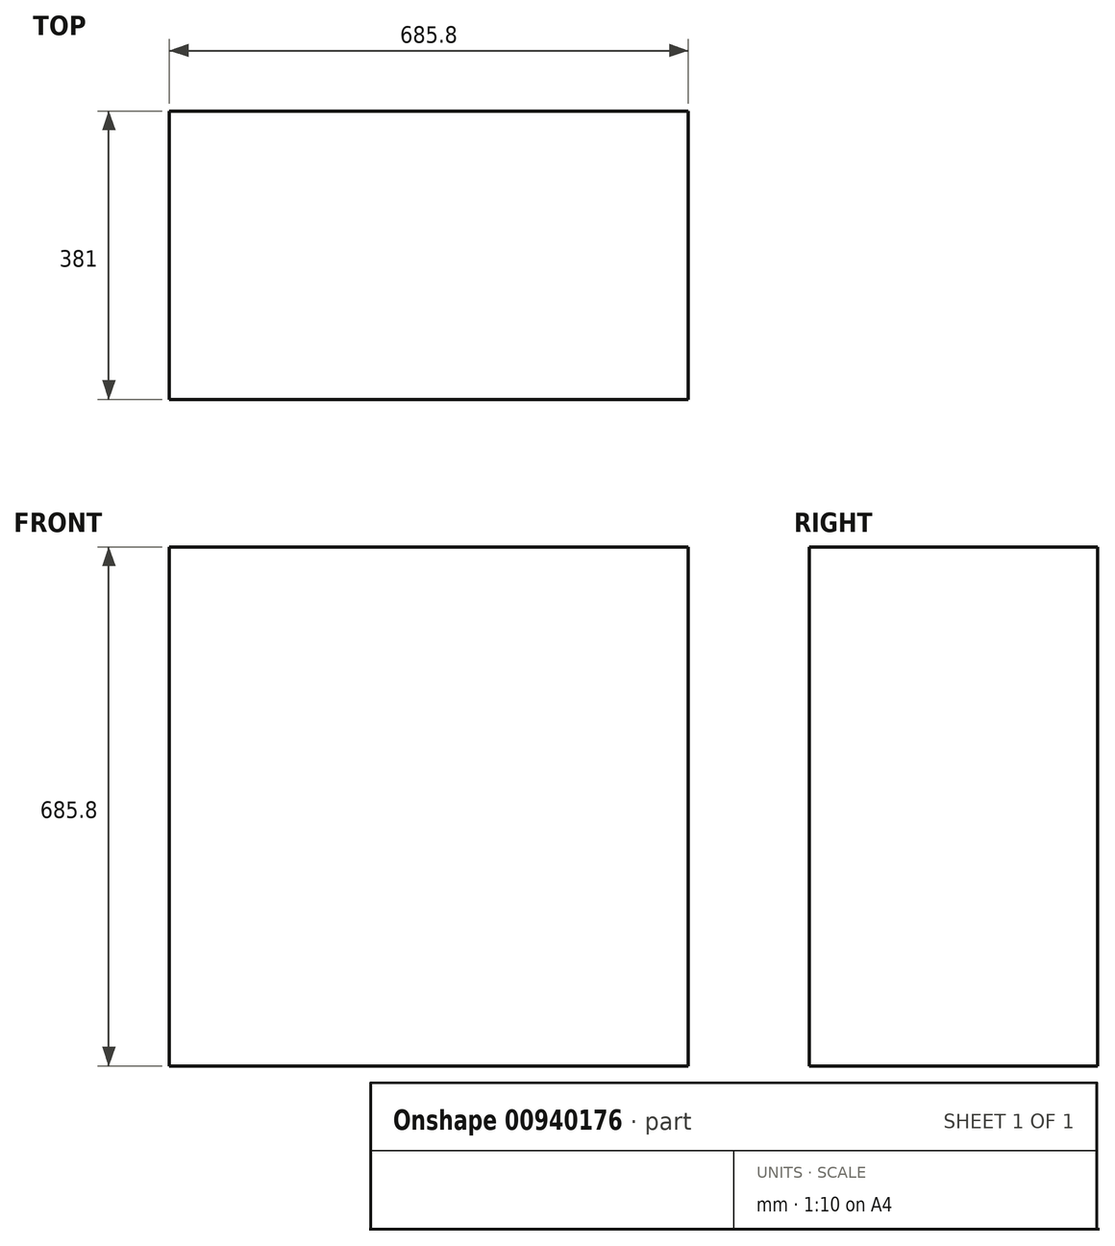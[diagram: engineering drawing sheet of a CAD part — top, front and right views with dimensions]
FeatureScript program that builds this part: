
annotation { "Feature Type Name" : "Feature", "Feature Type Description" : "" }
export const myFeature = defineFeature(function(context is Context, id is Id, definition is map)
    precondition{}
    {
        {
            var Q0;
            Q0=qCreatedBy(makeId("Top.planeOp"),FACE);
            var sketch = newSketch(context, id + "F0", { "sketchPlane" : qUnion([Q0])});
            skLineSegment(sketch, "E0.bottom", {"start": v(-338.15, 137.94) * mm, "end": v(347.65, 137.94) * mm});
            skLineSegment(sketch, "E0.top", {"start": v(-338.15, -243.06) * mm, "end": v(347.65, -243.06) * mm});
            skLineSegment(sketch, "E0.left", {"start": v(-338.15, 137.94) * mm, "end": v(-338.15, -243.06) * mm});
            skLineSegment(sketch, "E0.right", {"start": v(347.65, 137.94) * mm, "end": v(347.65, -243.06) * mm});
            skSolve(sketch);
        }
        {
            var Q0;
            Q0=makeQuery(id+"F0.imprint","IMPRINT",FACE,{"disambiguationData":[TD([[makeQuery(id+"F0.imprint","IMPRINT",EDGE,{"derivedFrom":sQuery(id+"F0.wireOp",EDGE,"E0.bottom")}),-1.0]])]});
            extrude(context, id + "F1", {"entities" : qUnion([Q0]), "depth" : 685.8 * mm, "offsetDistance" : 25.4 * mm});
        }
    });
